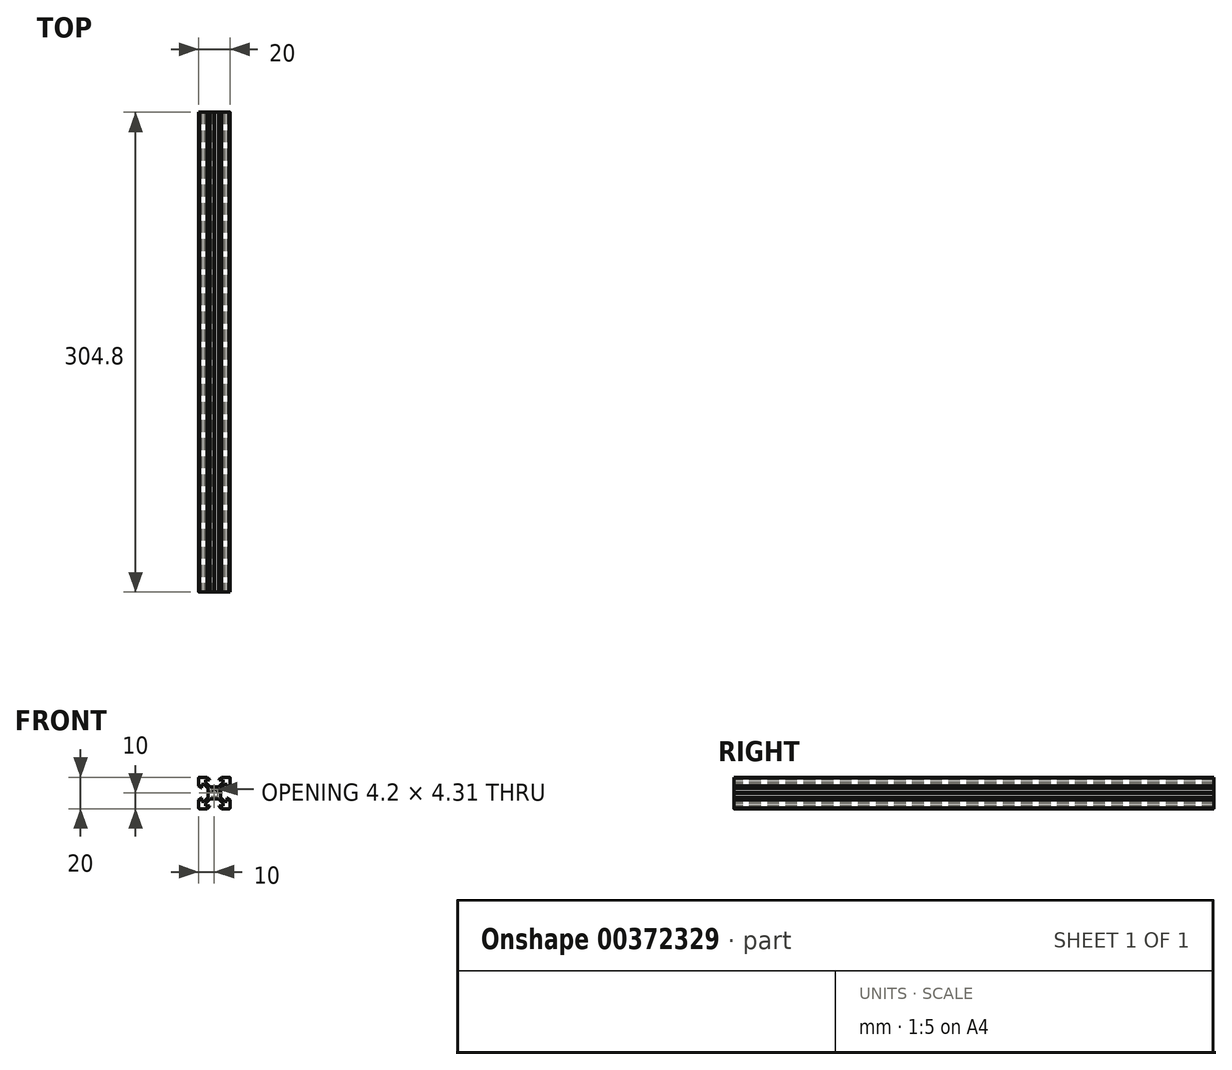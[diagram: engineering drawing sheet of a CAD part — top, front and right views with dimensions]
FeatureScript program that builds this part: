
annotation { "Feature Type Name" : "Feature", "Feature Type Description" : "" }
export const myFeature = defineFeature(function(context is Context, id is Id, definition is map)
    precondition{}
    {
        {
            var Q0;
            Q0=qCreatedBy(makeId("Front.planeOp"),FACE);
            var sketch = newSketch(context, id + "F0", { "sketchPlane" : qUnion([Q0])});
            skFitSpline(sketch, "E0.0", {"points": [v(-8.2, 3.13) * mm, v(-8.2, 3.92) * mm, v(-8.2, 4.7) * mm, v(-8.2, 5.5) * mm]});
            skFitSpline(sketch, "E0.1", {"points": [v(-8.2, 5.5) * mm, v(-7.65, 5.5) * mm, v(-7.1, 5.5) * mm, v(-6.56, 5.5) * mm]});
            skFitSpline(sketch, "E0.2", {"points": [v(-6.56, 5.5) * mm, v(-5.67, 4.61) * mm, v(-4.79, 3.73) * mm, v(-3.9, 2.84) * mm]});
            skFitSpline(sketch, "E0.3", {"points": [v(-2.84, 3.9) * mm, v(-3.73, 4.79) * mm, v(-4.61, 5.67) * mm, v(-5.5, 6.56) * mm]});
            skFitSpline(sketch, "E0.4", {"points": [v(-5.5, 6.56) * mm, v(-5.5, 7.1) * mm, v(-5.5, 7.65) * mm, v(-5.5, 8.2) * mm]});
            skFitSpline(sketch, "E0.5", {"points": [v(-5.5, 8.2) * mm, v(-4.7, 8.2) * mm, v(-3.92, 8.2) * mm, v(-3.12, 8.2) * mm]});
            skFitSpline(sketch, "E0.6", {"points": [v(-3.12, 8.2) * mm, v(-3.12, 8.32) * mm, v(-3.12, 8.43) * mm, v(-3.12, 8.55) * mm]});
            skFitSpline(sketch, "E0.7", {"points": [v(-10, 4.58) * mm, v(-9.51, 4.1) * mm, v(-9.03, 3.61) * mm, v(-8.54, 3.13) * mm]});
            skFitSpline(sketch, "E0.8", {"points": [v(-8.54, 3.13) * mm, v(-8.43, 3.13) * mm, v(-8.31, 3.13) * mm, v(-8.2, 3.13) * mm]});
            skFitSpline(sketch, "E0.9", {"points": [v(-10, 9.5) * mm, v(-10, 7.86) * mm, v(-10, 6.22) * mm, v(-10, 4.58) * mm]});
            skFitSpline(sketch, "E0.10", {"points": [v(-9.5, 10) * mm, v(-9.57, 10) * mm, v(-9.63, 9.99) * mm, v(-9.7, 9.96) * mm, v(-9.75, 9.94) * mm, v(-9.8, 9.9) * mm, v(-9.85, 9.85) * mm, v(-9.9, 9.8) * mm, v(-9.94, 9.75) * mm, v(-9.96, 9.7) * mm, v(-9.99, 9.63) * mm, v(-10, 9.57) * mm, v(-10, 9.5) * mm]});
            skFitSpline(sketch, "E0.11", {"points": [v(-4.58, 10) * mm, v(-6.22, 10) * mm, v(-7.86, 10) * mm, v(-9.5, 10) * mm]});
            skFitSpline(sketch, "E0.12", {"points": [v(-3.9, 2.84) * mm, v(-3.9, 1.96) * mm, v(-3.9, 1.09) * mm, v(-3.9, 0.21) * mm]});
            skFitSpline(sketch, "E0.13", {"points": [v(-3.9, 0.21) * mm, v(-3.83, 0.14) * mm, v(-3.76, 0.07) * mm, v(-3.69, 0) * mm]});
            skFitSpline(sketch, "E0.14", {"points": [v(-0.2, 3.9) * mm, v(-1.09, 3.9) * mm, v(-1.96, 3.9) * mm, v(-2.84, 3.9) * mm]});
            skFitSpline(sketch, "E0.15", {"points": [v(0, 3.7) * mm, v(-0.07, 3.76) * mm, v(-0.14, 3.83) * mm, v(-0.2, 3.9) * mm]});
            skFitSpline(sketch, "E0.16", {"points": [v(2.1, 0) * mm, v(2.1, 0.27) * mm, v(2, 0.82) * mm, v(1.52, 1.52) * mm, v(0.82, 2) * mm, v(0, 2.15) * mm, v(-0.82, 2) * mm, v(-1.52, 1.52) * mm, v(-2, 0.82) * mm, v(-2.1, 0.27) * mm, v(-2.1, 0) * mm]});
            skFitSpline(sketch, "E1.0", {"points": [v(-8.2, 3.13) * mm, v(-8.2, 3.92) * mm, v(-8.2, 4.7) * mm, v(-8.2, 5.5) * mm]});
            skFitSpline(sketch, "E1.1", {"points": [v(-8.2, 5.5) * mm, v(-7.65, 5.5) * mm, v(-7.1, 5.5) * mm, v(-6.56, 5.5) * mm]});
            skFitSpline(sketch, "E1.2", {"points": [v(-6.56, 5.5) * mm, v(-5.67, 4.61) * mm, v(-4.79, 3.73) * mm, v(-3.9, 2.84) * mm]});
            skFitSpline(sketch, "E1.3", {"points": [v(-2.84, 3.9) * mm, v(-3.73, 4.79) * mm, v(-4.61, 5.67) * mm, v(-5.5, 6.56) * mm]});
            skFitSpline(sketch, "E1.4", {"points": [v(-5.5, 6.56) * mm, v(-5.5, 7.1) * mm, v(-5.5, 7.65) * mm, v(-5.5, 8.2) * mm]});
            skFitSpline(sketch, "E1.5", {"points": [v(-5.5, 8.2) * mm, v(-4.7, 8.2) * mm, v(-3.92, 8.2) * mm, v(-3.12, 8.2) * mm]});
            skFitSpline(sketch, "E1.6", {"points": [v(-3.12, 8.2) * mm, v(-3.12, 8.32) * mm, v(-3.12, 8.43) * mm, v(-3.12, 8.55) * mm]});
            skFitSpline(sketch, "E1.7", {"points": [v(-10, 4.58) * mm, v(-9.51, 4.1) * mm, v(-9.03, 3.61) * mm, v(-8.54, 3.13) * mm]});
            skFitSpline(sketch, "E1.8", {"points": [v(-8.54, 3.13) * mm, v(-8.43, 3.13) * mm, v(-8.31, 3.13) * mm, v(-8.2, 3.13) * mm]});
            skFitSpline(sketch, "E1.9", {"points": [v(-10, 9.5) * mm, v(-10, 7.86) * mm, v(-10, 6.22) * mm, v(-10, 4.58) * mm]});
            skFitSpline(sketch, "E1.10", {"points": [v(-9.5, 10) * mm, v(-9.57, 10) * mm, v(-9.63, 9.99) * mm, v(-9.7, 9.96) * mm, v(-9.75, 9.94) * mm, v(-9.8, 9.9) * mm, v(-9.85, 9.85) * mm, v(-9.9, 9.8) * mm, v(-9.94, 9.75) * mm, v(-9.96, 9.7) * mm, v(-9.99, 9.63) * mm, v(-10, 9.57) * mm, v(-10, 9.5) * mm]});
            skFitSpline(sketch, "E1.11", {"points": [v(-4.58, 10) * mm, v(-6.22, 10) * mm, v(-7.86, 10) * mm, v(-9.5, 10) * mm]});
            skFitSpline(sketch, "E1.12", {"points": [v(-3.9, 2.84) * mm, v(-3.9, 1.96) * mm, v(-3.9, 1.09) * mm, v(-3.9, 0.21) * mm]});
            skFitSpline(sketch, "E1.13", {"points": [v(-3.9, 0.21) * mm, v(-3.83, 0.14) * mm, v(-3.76, 0.07) * mm, v(-3.69, 0) * mm]});
            skFitSpline(sketch, "E1.14", {"points": [v(-0.2, 3.9) * mm, v(-1.09, 3.9) * mm, v(-1.96, 3.9) * mm, v(-2.84, 3.9) * mm]});
            skFitSpline(sketch, "E1.15", {"points": [v(0, 3.7) * mm, v(-0.07, 3.76) * mm, v(-0.14, 3.83) * mm, v(-0.2, 3.9) * mm]});
            skFitSpline(sketch, "E1.16", {"points": [v(2.1, 0) * mm, v(2.1, 0.27) * mm, v(2, 0.82) * mm, v(1.52, 1.52) * mm, v(0.82, 2) * mm, v(0, 2.15) * mm, v(-0.82, 2) * mm, v(-1.52, 1.52) * mm, v(-2, 0.82) * mm, v(-2.1, 0.27) * mm, v(-2.1, 0) * mm]});
            skFitSpline(sketch, "E2.0", {"points": [v(2.84, 3.9) * mm, v(1.96, 3.9) * mm, v(1.09, 3.9) * mm, v(0.21, 3.9) * mm]});
            skFitSpline(sketch, "E2.1", {"points": [v(0.21, 3.9) * mm, v(0.14, 3.83) * mm, v(0.07, 3.76) * mm, v(0, 3.7) * mm]});
            skFitSpline(sketch, "E2.2", {"points": [v(3.9, 0.2) * mm, v(3.9, 1.09) * mm, v(3.9, 1.96) * mm, v(3.9, 2.84) * mm]});
            skFitSpline(sketch, "E2.3", {"points": [v(3.69, 0) * mm, v(3.76, 0.07) * mm, v(3.83, 0.14) * mm, v(3.9, 0.2) * mm]});
            skFitSpline(sketch, "E2.4", {"points": [v(3.9, 2.84) * mm, v(4.79, 3.73) * mm, v(5.67, 4.61) * mm, v(6.56, 5.5) * mm]});
            skFitSpline(sketch, "E2.5", {"points": [v(5.5, 6.56) * mm, v(4.61, 5.67) * mm, v(3.73, 4.79) * mm, v(2.84, 3.9) * mm]});
            skFitSpline(sketch, "E2.6", {"points": [v(6.56, 5.5) * mm, v(7.1, 5.5) * mm, v(7.65, 5.5) * mm, v(8.2, 5.5) * mm]});
            skFitSpline(sketch, "E2.7", {"points": [v(8.2, 5.5) * mm, v(8.2, 4.7) * mm, v(8.2, 3.92) * mm, v(8.2, 3.13) * mm]});
            skFitSpline(sketch, "E2.8", {"points": [v(8.2, 3.13) * mm, v(8.31, 3.13) * mm, v(8.43, 3.13) * mm, v(8.54, 3.13) * mm]});
            skFitSpline(sketch, "E2.9", {"points": [v(8.54, 3.13) * mm, v(9.03, 3.61) * mm, v(9.51, 4.1) * mm, v(10, 4.58) * mm]});
            skFitSpline(sketch, "E2.10", {"points": [v(10, 4.58) * mm, v(10, 6.22) * mm, v(10, 7.86) * mm, v(10, 9.5) * mm]});
            skFitSpline(sketch, "E2.11", {"points": [v(5.5, 8.2) * mm, v(5.5, 7.65) * mm, v(5.5, 7.1) * mm, v(5.5, 6.56) * mm]});
            skFitSpline(sketch, "E2.12", {"points": [v(3.13, 8.2) * mm, v(3.92, 8.2) * mm, v(4.7, 8.2) * mm, v(5.5, 8.2) * mm]});
            skFitSpline(sketch, "E2.13", {"points": [v(3.13, 8.55) * mm, v(3.13, 8.43) * mm, v(3.13, 8.32) * mm, v(3.13, 8.2) * mm]});
            skFitSpline(sketch, "E2.14", {"points": [v(9.5, 10) * mm, v(7.86, 10) * mm, v(6.22, 10) * mm, v(4.58, 10) * mm]});
            skFitSpline(sketch, "E2.15", {"points": [v(10, 9.5) * mm, v(10, 9.57) * mm, v(9.99, 9.63) * mm, v(9.96, 9.7) * mm, v(9.94, 9.75) * mm, v(9.9, 9.8) * mm, v(9.85, 9.85) * mm, v(9.8, 9.9) * mm, v(9.75, 9.94) * mm, v(9.7, 9.96) * mm, v(9.63, 9.99) * mm, v(9.57, 10) * mm, v(9.5, 10) * mm]});
            skFitSpline(sketch, "E2.16", {"points": [v(4.58, 10) * mm, v(4.1, 9.52) * mm, v(3.61, 9.03) * mm, v(3.13, 8.55) * mm]});
            skLineSegment(sketch, "E3", {"start": v(-4.58, 10) * mm, "end": v(-3.12, 8.55) * mm});
            skFitSpline(sketch, "E4.MirrorCS", {"points": [v(-3.9, -0.2) * mm, v(-3.83, -0.14) * mm, v(-3.76, -0.07) * mm, v(-3.69, 0) * mm]});
            skFitSpline(sketch, "E5.MirrorCS", {"points": [v(0, -3.7) * mm, v(-0.07, -3.76) * mm, v(-0.14, -3.83) * mm, v(-0.21, -3.9) * mm]});
            skFitSpline(sketch, "E6.MirrorCS", {"points": [v(-8.55, -3.12) * mm, v(-8.43, -3.12) * mm, v(-8.32, -3.12) * mm, v(-8.2, -3.12) * mm]});
            skFitSpline(sketch, "E7.MirrorCS", {"points": [v(0.2, -3.9) * mm, v(0.14, -3.83) * mm, v(0.07, -3.76) * mm, v(0, -3.7) * mm]});
            skFitSpline(sketch, "E8.MirrorCS", {"points": [v(-3.13, -8.2) * mm, v(-3.13, -8.31) * mm, v(-3.13, -8.43) * mm, v(-3.13, -8.54) * mm]});
            skFitSpline(sketch, "E9.MirrorCS", {"points": [v(-3.9, -0.2) * mm, v(-3.83, -0.14) * mm, v(-3.76, -0.07) * mm, v(-3.69, 0) * mm]});
            skFitSpline(sketch, "E10.MirrorCS", {"points": [v(-8.55, -3.12) * mm, v(-8.43, -3.12) * mm, v(-8.32, -3.12) * mm, v(-8.2, -3.12) * mm]});
            skFitSpline(sketch, "E11.MirrorCS", {"points": [v(0, -3.7) * mm, v(-0.07, -3.76) * mm, v(-0.14, -3.83) * mm, v(-0.21, -3.9) * mm]});
            skFitSpline(sketch, "E12.MirrorCS", {"points": [v(-3.13, -8.2) * mm, v(-3.13, -8.31) * mm, v(-3.13, -8.43) * mm, v(-3.13, -8.54) * mm]});
            skFitSpline(sketch, "E13.MirrorCS", {"points": [v(3.12, -8.55) * mm, v(3.12, -8.43) * mm, v(3.12, -8.32) * mm, v(3.12, -8.2) * mm]});
            skFitSpline(sketch, "E14.MirrorCS", {"points": [v(3.69, 0) * mm, v(3.76, -0.07) * mm, v(3.83, -0.14) * mm, v(3.9, -0.21) * mm]});
            skFitSpline(sketch, "E15.MirrorCS", {"points": [v(8.2, -3.13) * mm, v(8.31, -3.13) * mm, v(8.43, -3.13) * mm, v(8.54, -3.13) * mm]});
            skFitSpline(sketch, "E16.MirrorCS", {"points": [v(-8.2, -5.5) * mm, v(-7.65, -5.5) * mm, v(-7.1, -5.5) * mm, v(-6.56, -5.5) * mm]});
            skFitSpline(sketch, "E17.MirrorCS", {"points": [v(-2.84, -3.9) * mm, v(-3.73, -4.79) * mm, v(-4.61, -5.67) * mm, v(-5.5, -6.56) * mm]});
            skFitSpline(sketch, "E18.MirrorCS", {"points": [v(-5.5, -8.2) * mm, v(-4.7, -8.2) * mm, v(-3.92, -8.2) * mm, v(-3.13, -8.2) * mm]});
            skFitSpline(sketch, "E19.MirrorCS", {"points": [v(-5.5, -6.56) * mm, v(-5.5, -7.1) * mm, v(-5.5, -7.65) * mm, v(-5.5, -8.2) * mm]});
            skFitSpline(sketch, "E20.MirrorCS", {"points": [v(-0.21, -3.9) * mm, v(-1.09, -3.9) * mm, v(-1.96, -3.9) * mm, v(-2.84, -3.9) * mm]});
            skFitSpline(sketch, "E21.MirrorCS", {"points": [v(-8.2, -3.12) * mm, v(-8.2, -3.92) * mm, v(-8.2, -4.7) * mm, v(-8.2, -5.5) * mm]});
            skFitSpline(sketch, "E22.MirrorCS", {"points": [v(-10, -4.58) * mm, v(-9.52, -4.1) * mm, v(-9.03, -3.6) * mm, v(-8.55, -3.12) * mm]});
            skFitSpline(sketch, "E23.MirrorCS", {"points": [v(-10, -9.5) * mm, v(-10, -7.86) * mm, v(-10, -6.22) * mm, v(-10, -4.58) * mm]});
            skFitSpline(sketch, "E24.MirrorCS", {"points": [v(-9.5, -10) * mm, v(-9.57, -10) * mm, v(-9.63, -9.99) * mm, v(-9.7, -9.96) * mm, v(-9.75, -9.94) * mm, v(-9.8, -9.9) * mm, v(-9.85, -9.85) * mm, v(-9.9, -9.8) * mm, v(-9.94, -9.75) * mm, v(-9.96, -9.7) * mm, v(-9.99, -9.63) * mm, v(-10, -9.57) * mm, v(-10, -9.5) * mm]});
            skFitSpline(sketch, "E25.MirrorCS", {"points": [v(-4.58, -10) * mm, v(-6.22, -10) * mm, v(-7.86, -10) * mm, v(-9.5, -10) * mm]});
            skFitSpline(sketch, "E26.MirrorCS", {"points": [v(-3.9, -2.84) * mm, v(-3.9, -1.96) * mm, v(-3.9, -1.09) * mm, v(-3.9, -0.21) * mm]});
            skFitSpline(sketch, "E27.MirrorCS", {"points": [v(-6.56, -5.5) * mm, v(-5.67, -4.61) * mm, v(-4.79, -3.73) * mm, v(-3.9, -2.84) * mm]});
            skFitSpline(sketch, "E28.MirrorCS", {"points": [v(2.1, 0) * mm, v(2.1, -0.27) * mm, v(2, -0.82) * mm, v(1.52, -1.52) * mm, v(0.82, -2) * mm, v(0, -2.15) * mm, v(-0.82, -2) * mm, v(-1.52, -1.52) * mm, v(-2, -0.82) * mm, v(-2.1, -0.27) * mm, v(-2.1, 0) * mm]});
            skFitSpline(sketch, "E29.MirrorCS", {"points": [v(4.58, -10) * mm, v(4.1, -9.52) * mm, v(3.6, -9.03) * mm, v(3.12, -8.55) * mm]});
            skFitSpline(sketch, "E30.MirrorCS", {"points": [v(-6.56, -5.5) * mm, v(-5.67, -4.61) * mm, v(-4.79, -3.73) * mm, v(-3.9, -2.84) * mm]});
            skFitSpline(sketch, "E31.MirrorCS", {"points": [v(10, -4.58) * mm, v(10, -6.22) * mm, v(10, -7.86) * mm, v(10, -9.5) * mm]});
            skLineSegment(sketch, "E32.MirrorCS", {"start": v(-4.58, -10) * mm, "end": v(-3.13, -8.54) * mm});
            skFitSpline(sketch, "E33.MirrorCS", {"points": [v(-4.58, -10) * mm, v(-6.22, -10) * mm, v(-7.86, -10) * mm, v(-9.5, -10) * mm]});
            skFitSpline(sketch, "E34.MirrorCS", {"points": [v(6.56, -5.5) * mm, v(7.1, -5.5) * mm, v(7.65, -5.5) * mm, v(8.2, -5.5) * mm]});
            skFitSpline(sketch, "E35.MirrorCS", {"points": [v(-10, -4.58) * mm, v(-9.52, -4.1) * mm, v(-9.03, -3.6) * mm, v(-8.55, -3.12) * mm]});
            skFitSpline(sketch, "E36.MirrorCS", {"points": [v(-5.5, -6.56) * mm, v(-5.5, -7.1) * mm, v(-5.5, -7.65) * mm, v(-5.5, -8.2) * mm]});
            skFitSpline(sketch, "E37.MirrorCS", {"points": [v(3.12, -8.2) * mm, v(3.92, -8.2) * mm, v(4.7, -8.2) * mm, v(5.5, -8.2) * mm]});
            skFitSpline(sketch, "E38.MirrorCS", {"points": [v(-8.2, -5.5) * mm, v(-7.65, -5.5) * mm, v(-7.1, -5.5) * mm, v(-6.56, -5.5) * mm]});
            skFitSpline(sketch, "E39.MirrorCS", {"points": [v(-8.2, -3.12) * mm, v(-8.2, -3.92) * mm, v(-8.2, -4.7) * mm, v(-8.2, -5.5) * mm]});
            skFitSpline(sketch, "E40.MirrorCS", {"points": [v(10, -9.5) * mm, v(10, -9.57) * mm, v(9.99, -9.63) * mm, v(9.96, -9.7) * mm, v(9.94, -9.75) * mm, v(9.9, -9.8) * mm, v(9.85, -9.85) * mm, v(9.8, -9.9) * mm, v(9.75, -9.94) * mm, v(9.7, -9.96) * mm, v(9.63, -9.99) * mm, v(9.57, -10) * mm, v(9.5, -10) * mm]});
            skFitSpline(sketch, "E41.MirrorCS", {"points": [v(2.1, 0) * mm, v(2.1, -0.27) * mm, v(2, -0.82) * mm, v(1.52, -1.52) * mm, v(0.82, -2) * mm, v(0, -2.15) * mm, v(-0.82, -2) * mm, v(-1.52, -1.52) * mm, v(-2, -0.82) * mm, v(-2.1, -0.27) * mm, v(-2.1, 0) * mm]});
            skFitSpline(sketch, "E42.MirrorCS", {"points": [v(2.84, -3.9) * mm, v(1.96, -3.9) * mm, v(1.09, -3.9) * mm, v(0.2, -3.9) * mm]});
            skFitSpline(sketch, "E43.MirrorCS", {"points": [v(-10, -9.5) * mm, v(-10, -7.86) * mm, v(-10, -6.22) * mm, v(-10, -4.58) * mm]});
            skFitSpline(sketch, "E44.MirrorCS", {"points": [v(8.2, -5.5) * mm, v(8.2, -4.7) * mm, v(8.2, -3.92) * mm, v(8.2, -3.13) * mm]});
            skFitSpline(sketch, "E45.MirrorCS", {"points": [v(8.54, -3.13) * mm, v(9.03, -3.61) * mm, v(9.51, -4.1) * mm, v(10, -4.58) * mm]});
            skFitSpline(sketch, "E46.MirrorCS", {"points": [v(3.9, -2.84) * mm, v(4.79, -3.73) * mm, v(5.67, -4.61) * mm, v(6.56, -5.5) * mm]});
            skFitSpline(sketch, "E47.MirrorCS", {"points": [v(-9.5, -10) * mm, v(-9.57, -10) * mm, v(-9.63, -9.99) * mm, v(-9.7, -9.96) * mm, v(-9.75, -9.94) * mm, v(-9.8, -9.9) * mm, v(-9.85, -9.85) * mm, v(-9.9, -9.8) * mm, v(-9.94, -9.75) * mm, v(-9.96, -9.7) * mm, v(-9.99, -9.63) * mm, v(-10, -9.57) * mm, v(-10, -9.5) * mm]});
            skFitSpline(sketch, "E48.MirrorCS", {"points": [v(-0.21, -3.9) * mm, v(-1.09, -3.9) * mm, v(-1.96, -3.9) * mm, v(-2.84, -3.9) * mm]});
            skFitSpline(sketch, "E49.MirrorCS", {"points": [v(5.5, -6.56) * mm, v(4.61, -5.67) * mm, v(3.73, -4.79) * mm, v(2.84, -3.9) * mm]});
            skFitSpline(sketch, "E50.MirrorCS", {"points": [v(-2.84, -3.9) * mm, v(-3.73, -4.79) * mm, v(-4.61, -5.67) * mm, v(-5.5, -6.56) * mm]});
            skFitSpline(sketch, "E51.MirrorCS", {"points": [v(-5.5, -8.2) * mm, v(-4.7, -8.2) * mm, v(-3.92, -8.2) * mm, v(-3.13, -8.2) * mm]});
            skFitSpline(sketch, "E52.MirrorCS", {"points": [v(5.5, -8.2) * mm, v(5.5, -7.65) * mm, v(5.5, -7.1) * mm, v(5.5, -6.56) * mm]});
            skFitSpline(sketch, "E53.MirrorCS", {"points": [v(3.9, -0.21) * mm, v(3.9, -1.09) * mm, v(3.9, -1.96) * mm, v(3.9, -2.84) * mm]});
            skFitSpline(sketch, "E54.MirrorCS", {"points": [v(-3.9, -2.84) * mm, v(-3.9, -1.96) * mm, v(-3.9, -1.09) * mm, v(-3.9, -0.21) * mm]});
            skFitSpline(sketch, "E55.MirrorCS", {"points": [v(9.5, -10) * mm, v(7.86, -10) * mm, v(6.22, -10) * mm, v(4.58, -10) * mm]});
            skLineSegment(sketch, "E56.MirrorCS", {"start": v(0, 3.7) * mm, "end": v(0, 0) * mm, "construction": true});
            skLineSegment(sketch, "E57.MirrorCS", {"start": v(0, -3.7) * mm, "end": v(0, 0) * mm, "construction": true});
            skSolve(sketch);
        }
        {
            var Q0;
            Q0 = qSketchRegion(id + "F0", true);
            extrude(context, id + "F1", {"entities" : qUnion([Q0]), "oppositeDirection" : true, "depth" : 304.8 * mm});
        }
    });
